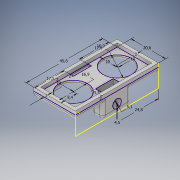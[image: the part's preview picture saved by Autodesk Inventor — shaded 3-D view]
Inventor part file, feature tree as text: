
AUTODESK INVENTOR PART (.ipt)
format: ipt  version: 2019 (Build 230136000, 136)  size: 296,960 bytes
history: native  units: mm
features: extrude x12, sketch x7, fillet x1
ambient origin geometry x8: Origin, YZ Plane, XZ Plane, XY Plane, X Axis, Y Axis, Z Axis, Center Point
bodies: Solid1 (feature_tree)
feature tree (20):
  sketch  "Sketch1"  dims[d0=45.6mm d1=20.6mm]
  extrude  "Extrusion1"  Depth=20.6mm
  extrude  "Extrusion2"  Depth=2.0mm
  extrude  "Extrusion4"  Depth=2.0mm
  extrude  "Extrusion5"  Depth=10.0mm
  extrude  "Extrusion6"  Depth=16.9mm
  extrude  "Extrusion7"  Depth=10.0mm
  extrude  "Extrusion8"  Depth=2.0mm
  sketch  "Sketch3"  dims[d4=2.0mm d5=2.0mm]
  extrude  "Extrusion9"  Depth=2.0mm
  extrude  "Extrusion10"  Depth=2.0mm
  sketch  "Sketch5"  dims[d8=9.4mm d9=16.9mm]
  extrude  "Extrusion11"  Depth=2.0mm TaperAngle=0.0deg
  extrude  "Extrusion12"  Depth=2.0mm TaperAngle=0.0deg
  extrude  "Extrusion13"  Depth=2.0mm TaperAngle=0.0deg
  fillet  "Fillet3"  Radius=5.0mm
  sketch  "Sketch2"  dims[d2=2.0mm d3=2.0mm]
  sketch  "Sketch4"  dims[d6=16.9mm d7=10.0mm]
  sketch  "Sketch6"  dims[d10=10.0mm d11=10.0mm]
  sketch  "Sketch7"  dims[d12=17.5mm d13=17.5mm d14=2.0mm d15=5.5mm d16=2.0mm d17=0.0mm d18=11.0mm d19=0.0mm d22=11.0mm d23=0.0mm d24=5.0mm d25=0.0mm d26=5.0mm d27=0.0mm d28=1.0mm d29=0.0mm d30=4.0mm d31=0.0mm d32=5.1mm d33=4.5mm d34=24.8mm d36=4.0mm d37=0.0mm d38=8.0mm d39=16.0mm d40=4.0mm d41=0.0mm d42=2.2mm d44=4.0mm d45=0.0mm d47=16.4mm d48=8.0mm d49=0.0mm d50=16.4mm d51=8.0mm d52=0.0mm d53=2.0mm]
